# Revit family: Shower_Arm-DXV-Sheppards_Hook-D3570131X_Series
name_source: partatom
category: Plumbing Fixtures
revit_build: Autodesk Revit 2014 (Build: 20130308_1515(x64)
units: mm (PartAtom-declared; Revit-internal decimal feet)

## types (8) — shared parameters
Assembly Code = D2010710
CW Connection = Yes
CWFU = 1.5
Cold Water Connection Diameter = 1/2"
Cold Water Connection Radius = 1/4"
Default Elevation = 74 3/4"
HW Connection = Yes
HWFU = 1.5
Hot Water Connection Diameter = 1"
Hot Water Connection Radius = 1/4"
Installation Type = Wall Mounted
Manufacturer = DXV
Price = Prices may vary. Please consult Manufacturer Representative for most up-to-date price list.
Product Documentation Link = https://dxv01.blob.core.windows.net
Product Page URL = https://www.dxv.com
Tempered Water Connection Diameter = 1/2"
Tempered Water Connection Radius = 1/4"
URL = https://www.dxv.com
Vent Connection = No
WFU = 2
Warranty Documentation Link = https://www.dxv.com
Waste Connection = No
Width = 2 1/8"

## per-type parameters (varying)
| type | Center to Spout End | Description | End to Center | Finish | Height | Length | Material |
| D35701312.100 | 3 1/4" | Shepherd's Hook 12 Shower Arm | 5 1/8" | Cast Brass-DXV-100-Polished Chrome | 7 5/8" | 12 5/8" | Cast Brass-DXV-100-Polished Chrome |
| D35701312.144 | 3 1/4" | Shepherd's Hook 12 Shower Arm | 5 1/8" | Cast Brass-DXV-144-Brushed Nickel | 7 5/8" | 12 5/8" | Cast Brass-DXV-144-Brushed Nickel |
| D35701312.150 | 3 1/4" | Shepherd's Hook 12 Shower Arm | 5 1/8" | Cast Brass-DXV-150-Platinum Nickel | 7 5/8" | 12 5/8" | Cast Brass-DXV-150-Platinum Nickel |
| D35701312.427 | 3 1/4" | Shepherd's Hook 12 Shower Arm | 5 1/8" | Cast Brass-DXV-427-Satin Brass | 7 5/8" | 12 5/8" | Cast Brass-DXV-427-Satin Brass |
| D35701316.100 | 4" | Shepherd's Hook 16 Shower Arm | 6 3/4" | Cast Brass-DXV-100-Polished Chrome | 9 5/8" | 16 5/8" | Cast Brass-DXV-100-Polished Chrome |
| D35701316.144 | 4" | Shepherd's Hook 16 Shower Arm | 6 3/4" | Cast Brass-DXV-144-Brushed Nickel | 9 5/8" | 16 5/8" | Cast Brass-DXV-144-Brushed Nickel |
| D35701316.150 | 4" | Shepherd's Hook 16 Shower Arm | 6 3/4" | Cast Brass-DXV-150-Platinum Nickel | 9 5/8" | 16 5/8" | Cast Brass-DXV-150-Platinum Nickel |
| D35701316.427 | 4" | Shepherd's Hook 16 Shower Arm | 6 3/4" | Cast Brass-DXV-427-Satin Brass | 9 5/8" | 16 5/8" | Cast Brass-DXV-427-Satin Brass |

note: column(s) folded — value = type name in every type: Model

## geometry (parser evidence)
native form markers: Sweep x3
no freeform markers — native parametric forms only
